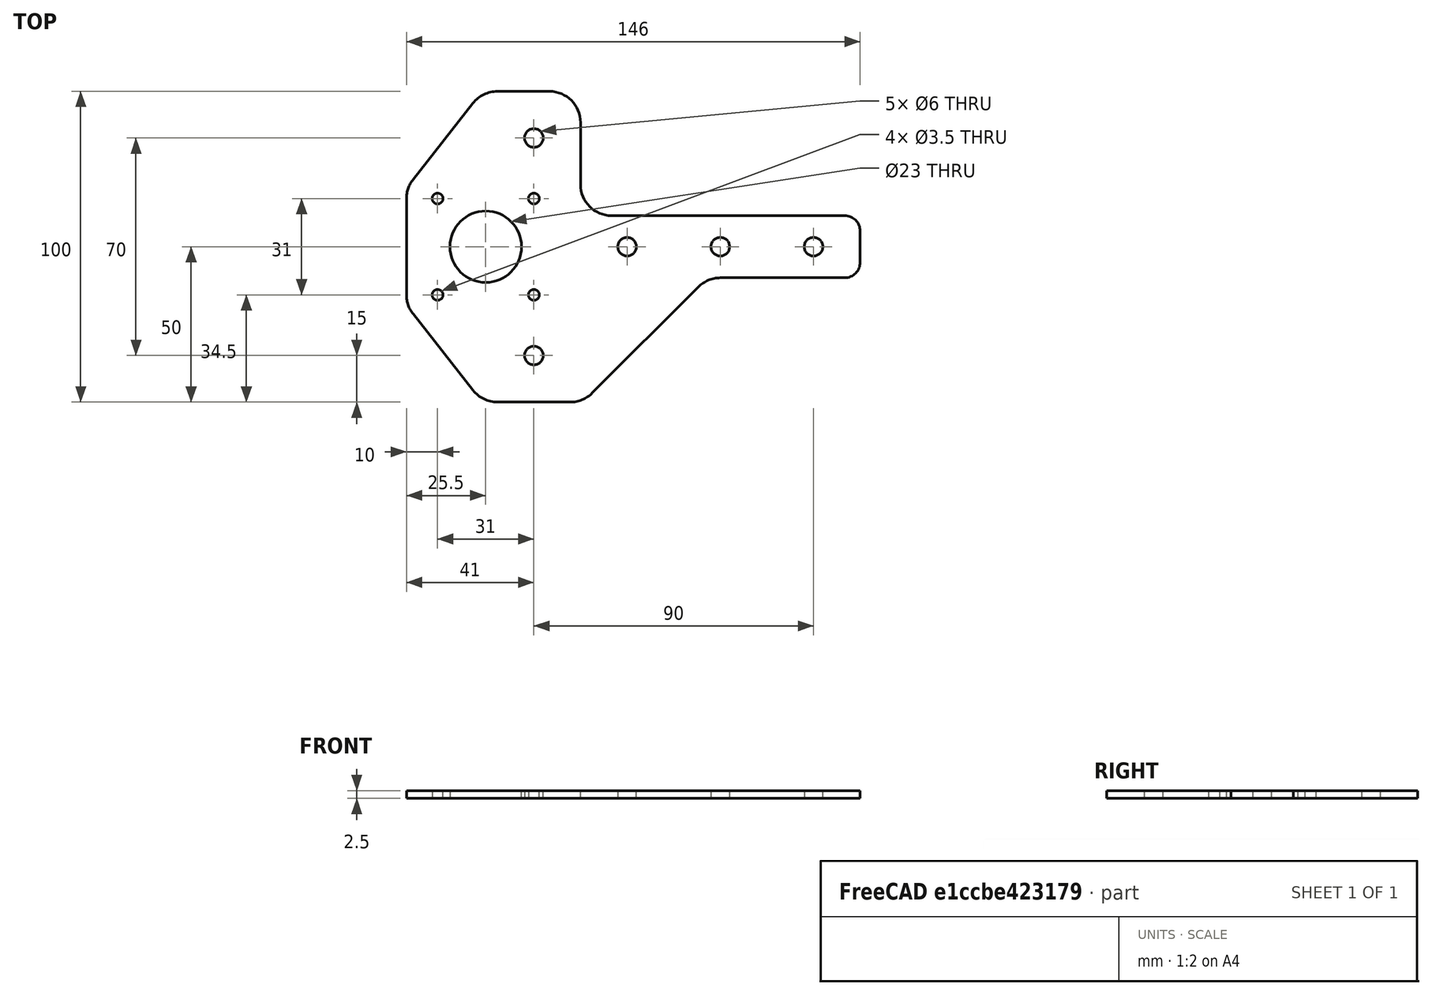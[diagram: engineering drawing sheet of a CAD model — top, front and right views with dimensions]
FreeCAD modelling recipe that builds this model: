
FCSTD DOCUMENT  (FreeCAD 0.19R24276 (Git))
Label: X_stepper_plate
License: All rights reserved
LicenseURL: http://en.wikipedia.org/wiki/All_rights_reserved
objects: Sketcher::SketchObject×1, PartDesign::Pad×1, PartDesign::Body×1
note: 4 computed .brp shape members not serialized (recipe doc carries the construction recipe); baked Part::Feature solids carry a one-line shape summary decoded from their .brp

FEATURE [Sketcher::SketchObject] Sketch
  FullyConstrained = true
  MapMode = 5
  Support = -> [XY_Plane]
  sketch-geometry (36):
    g0: Circle CenterX=0 CenterY=0 CenterZ=0 NormalX=0 NormalY=0 NormalZ=1 AngleXU=0 Radius=11.5
    g1: LineSegment StartX=-15.5 StartY=15.5 StartZ=0 EndX=15.5 EndY=15.5 EndZ=0
    g2: LineSegment StartX=15.5 StartY=15.5 StartZ=0 EndX=15.5 EndY=-15.5 EndZ=0
    g3: LineSegment StartX=15.5 StartY=-15.5 StartZ=0 EndX=-15.5 EndY=-15.5 EndZ=0
    g4: LineSegment StartX=-15.5 StartY=-15.5 StartZ=0 EndX=-15.5 EndY=15.5 EndZ=0
    g5: Circle CenterX=-15.5 CenterY=15.5 CenterZ=0 NormalX=0 NormalY=0 NormalZ=1 AngleXU=0 Radius=1.75
    g6: Circle CenterX=15.5 CenterY=15.5 CenterZ=0 NormalX=0 NormalY=0 NormalZ=1 AngleXU=0 Radius=1.75
    g7: Circle CenterX=15.5 CenterY=-15.5 CenterZ=0 NormalX=0 NormalY=0 NormalZ=1 AngleXU=0 Radius=1.75
    g8: Circle CenterX=-15.5 CenterY=-15.5 CenterZ=0 NormalX=0 NormalY=0 NormalZ=1 AngleXU=0 Radius=1.75
    g9: Circle CenterX=45.5 CenterY=0 CenterZ=0 NormalX=0 NormalY=0 NormalZ=1 AngleXU=0 Radius=3
    g10: Circle CenterX=75.5 CenterY=0 CenterZ=0 NormalX=0 NormalY=0 NormalZ=1 AngleXU=0 Radius=3
    g11: Circle CenterX=105.5 CenterY=0 CenterZ=0 NormalX=0 NormalY=0 NormalZ=1 AngleXU=0 Radius=3
    g12: LineSegment StartX=15.5 StartY=50 StartZ=0 EndX=15.5 EndY=-50 EndZ=0
    g13: Circle CenterX=15.5 CenterY=35 CenterZ=0 NormalX=0 NormalY=0 NormalZ=1 AngleXU=0 Radius=3
    g14: Circle CenterX=15.5 CenterY=-35 CenterZ=0 NormalX=0 NormalY=0 NormalZ=1 AngleXU=0 Radius=3
    g15: LineSegment StartX=-25.5 StartY=15.5 StartZ=0 EndX=-25.5 EndY=-15.5 EndZ=0
    g16: LineSegment StartX=-23.3578 StartY=-21.685 StartZ=0 EndX=-4.07357 EndY=-46.185 EndZ=0
    g17: LineSegment StartX=3.78427 StartY=-50 StartZ=0 EndX=27.2157 EndY=-50 EndZ=0
    g18: LineSegment StartX=34.2868 StartY=-47.0711 StartZ=0 EndX=68.4289 EndY=-12.9289 EndZ=0
    g19: LineSegment StartX=75.5 StartY=-10 StartZ=0 EndX=115.5 EndY=-10 EndZ=0
    g20: LineSegment StartX=120.5 StartY=-5 StartZ=0 EndX=120.5 EndY=5 EndZ=0
    g21: LineSegment StartX=115.5 StartY=10 StartZ=0 EndX=40.5 EndY=10 EndZ=0
    g22: LineSegment StartX=30.5 StartY=20 StartZ=0 EndX=30.5 EndY=40 EndZ=0
    g23: LineSegment StartX=20.5 StartY=50 StartZ=0 EndX=3.78427 EndY=50 EndZ=0
    g24: LineSegment StartX=-4.07357 StartY=46.185 StartZ=0 EndX=-23.3578 EndY=21.685 EndZ=0
    g25: ArcOfCircle CenterX=115.5 CenterY=5 CenterZ=0 NormalX=0 NormalY=0 NormalZ=1 AngleXU=0 Radius=5 StartAngle=0 EndAngle=1.5708
    g26: ArcOfCircle CenterX=115.5 CenterY=-5 CenterZ=0 NormalX=0 NormalY=0 NormalZ=1 AngleXU=0 Radius=5 StartAngle=4.71239 EndAngle=6.28319
    g27: ArcOfCircle CenterX=75.5 CenterY=-20 CenterZ=0 NormalX=0 NormalY=0 NormalZ=1 AngleXU=0 Radius=10 StartAngle=1.5708 EndAngle=2.35619
    g28: ArcOfCircle CenterX=27.2157 CenterY=-40 CenterZ=0 NormalX=0 NormalY=0 NormalZ=1 AngleXU=0 Radius=10 StartAngle=4.71239 EndAngle=5.49779
    g29: ArcOfCircle CenterX=3.78427 CenterY=-40 CenterZ=0 NormalX=0 NormalY=0 NormalZ=1 AngleXU=0 Radius=10 StartAngle=3.80843 EndAngle=4.71239
    g30: ArcOfCircle CenterX=-15.5 CenterY=-15.5 CenterZ=0 NormalX=0 NormalY=0 NormalZ=1 AngleXU=0 Radius=10 StartAngle=3.14159 EndAngle=3.80843
    g31: ArcOfCircle CenterX=-15.5 CenterY=15.5 CenterZ=0 NormalX=0 NormalY=0 NormalZ=1 AngleXU=0 Radius=10 StartAngle=2.47476 EndAngle=3.14159
    g32: ArcOfCircle CenterX=3.78427 CenterY=40 CenterZ=0 NormalX=0 NormalY=0 NormalZ=1 AngleXU=0 Radius=10 StartAngle=1.5708 EndAngle=2.47476
    g33: ArcOfCircle CenterX=20.5 CenterY=40 CenterZ=0 NormalX=0 NormalY=0 NormalZ=1 AngleXU=0 Radius=10 StartAngle=2e-16 EndAngle=1.5708
    g34: ArcOfCircle CenterX=40.5 CenterY=20 CenterZ=0 NormalX=0 NormalY=0 NormalZ=1 AngleXU=0 Radius=10 StartAngle=3.14159 EndAngle=4.71239
    g35: LineSegment StartX=75.5 StartY=10 StartZ=0 EndX=75.5 EndY=-10 EndZ=0
  constraints (88):
    c: Coincident(g0,g-1)
    c: Coincident(g1,g2)
    c: Coincident(g2,g3)
    c: Coincident(g3,g4)
    c: Coincident(g4,g1)
    c: Horizontal(g1)
    c: Horizontal(g3)
    c: Vertical(g2)
    c: Vertical(g4)
    c: Coincident(g5,g1)
    c: Coincident(g6,g1)
    c: Coincident(g7,g2)
    c: Coincident(g8,g3)
    c: PointOnObject(g9,g-1)
    c: PointOnObject(g10,g-1)
    c: PointOnObject(g11,g-1)
    c: Equal(g9,g10)
    c: Equal(g10,g11)
    c: Equal(g6,g5)
    c: Equal(g5,g8)
    c: Equal(g8,g7)
    c: Vertical(g12)
    c: PointOnObject(g6,g12)
    c: Equal(g1,g2)
    c: Symmetric(g5,g7,g0)
    c: PointOnObject(g13,g12)
    c: Equal(g13,g14)
    c: Equal(g14,g9)
    c: Diameter(g13) = 6
    c: Diameter(g6) = 3.5
    c: DistanceX(g1,g1) = 31
    c: Vertical(g15)
    c: Horizontal(g19)
    c: Vertical(g20)
    c: Horizontal(g21)
    c: Vertical(g22)
    c: Horizontal(g23)
    c: Tangent(g20,g25) = -1.5708
    c: Tangent(g21,g25) = -1.5708
    c: Tangent(g19,g26) = -1.5708
    c: Tangent(g20,g26) = -1.5708
    c: Tangent(g18,g27) = 1.5708
    c: Tangent(g19,g27) = 1.5708
    c: Tangent(g17,g28) = -1.5708
    c: Tangent(g18,g28) = -1.5708
    c: Tangent(g16,g29) = -1.5708
    c: Tangent(g17,g29) = -1.5708
    c: Tangent(g15,g30) = -1.5708
    c: Tangent(g16,g30) = -1.5708
    c: Tangent(g15,g31) = -1.5708
    c: Tangent(g24,g31) = -1.5708
    c: Tangent(g23,g32) = -1.5708
    c: Tangent(g24,g32) = -1.5708
    c: Tangent(g22,g33) = -1.5708
    c: Tangent(g23,g33) = -1.5708
    c: Tangent(g21,g34) = 1.5708
    c: Tangent(g22,g34) = 1.5708
    c: Equal(g25,g26)
    c: Diameter(g25) = 10
    c: DistanceY(g19,g21) = 20
    c: DistanceX(g9,g10) = 30
    c: DistanceX(g10,g11) = 30
    c: DistanceX(g11,g20) = 15
    c: DistanceY(g0,g21) = 10
    c: DistanceY(g14,g13) = 70
    c: Symmetric(g31,g30,g-1)
    c: Symmetric(g14,g13,g-1)
    c: Symmetric(g16,g24,g-1)
    c: Equal(g32,g29)
    c: Diameter(g0) = 23
    c: Equal(g34,g33)
    c: DistanceY(g17,g23) = 100
    c: DistanceX(g14,g10) = 60
    c: Coincident(g30,g8)
    c: DistanceX(g13,g22) = 15
    c: Diameter(g34) = 20
    c: DistanceX(g15,g8) = 10
    c: Equal(g29,g30)
    c: PointOnObject(g35,g21)
    c: Coincident(g35,g19)
    c: Vertical(g35)
    c: PointOnObject(g10,g35)
    c: Symmetric(g17,g17,g12)
    c: Angle(g18,g17) = 2.35619
    c: PointOnObject(g12,g23)
    c: PointOnObject(g12,g17)
    c: Radius(g27) = 10
    c: Equal(g27,g28)
FEATURE [PartDesign::Pad] Pad
  Direction = (1,1,1)
  Length = 2.5
  Length2 = 100
  Profile = -> Sketch
  Type = 0
FEATURE [PartDesign::Body] Body
  Group = -> [Sketch,Pad]
  Origin = -> Origin
  Tip = -> Pad
